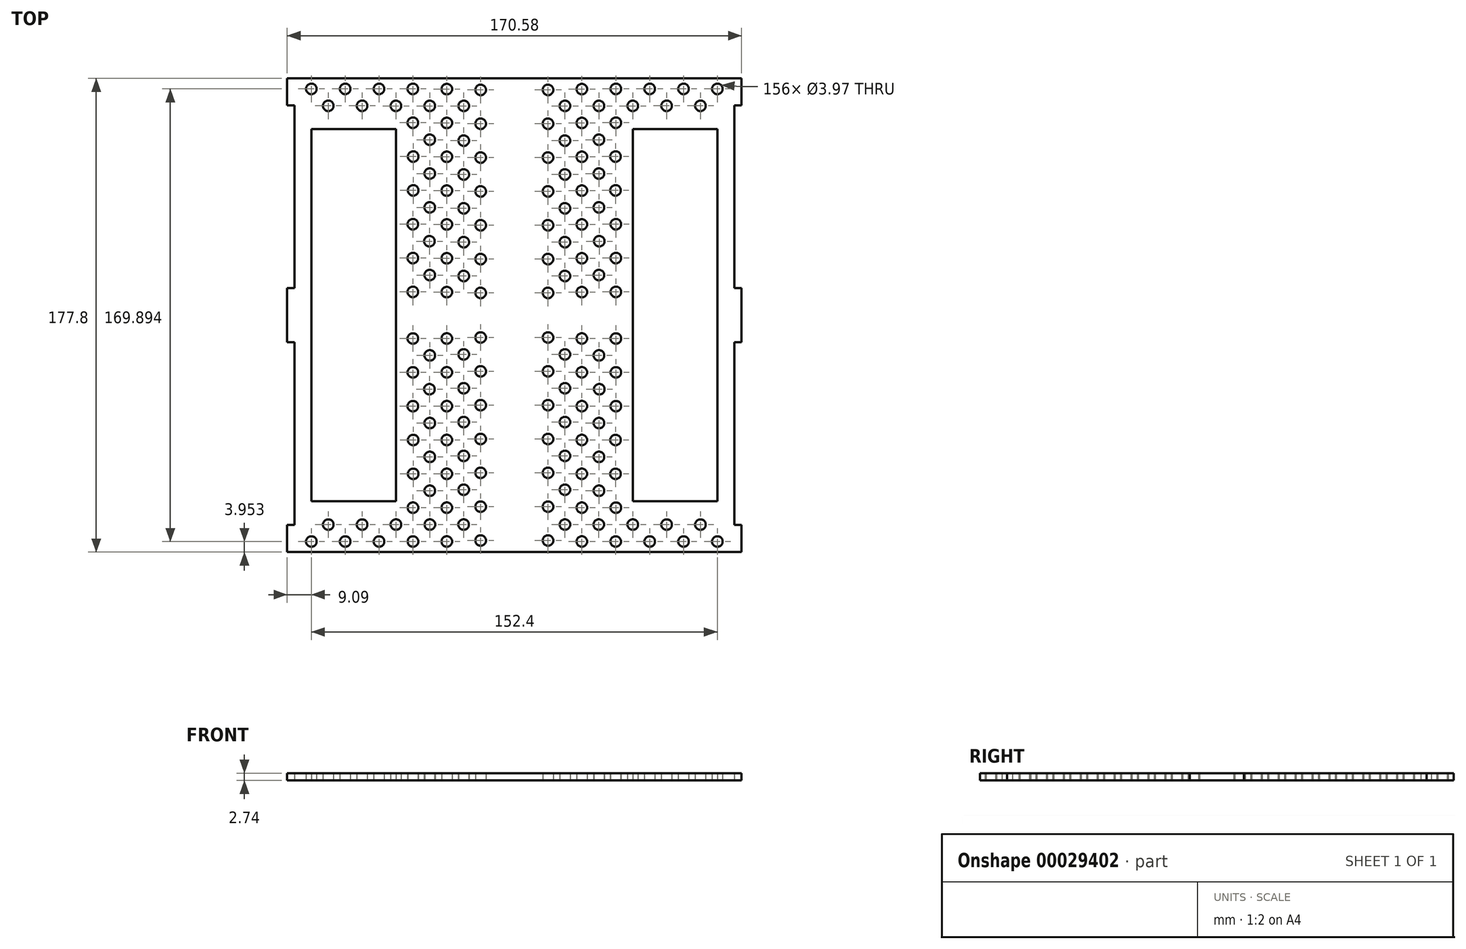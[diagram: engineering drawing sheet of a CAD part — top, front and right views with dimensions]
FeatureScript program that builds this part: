
annotation { "Feature Type Name" : "Feature", "Feature Type Description" : "" }
export const myFeature = defineFeature(function(context is Context, id is Id, definition is map)
    precondition{}
    {
        {
            var Q0;
            Q0=qCreatedBy(makeId("Top.planeOp"),FACE);
            var sketch = newSketch(context, id + "F0", { "sketchPlane" : qUnion([Q0])});
            skLineSegment(sketch, "E0.top", {"start": v(-63.5, -88.9) * mm, "end": v(19.05, -88.9) * mm});
            skLineSegment(sketch, "E1", {"start": v(-63.5, -88.9) * mm, "end": v(-66.24, -88.9) * mm});
            skLineSegment(sketch, "E2", {"start": v(-66.24, -88.9) * mm, "end": v(-66.24, -78.74) * mm});
            skLineSegment(sketch, "E3", {"start": v(-66.24, -78.74) * mm, "end": v(-63.5, -78.74) * mm});
            skLineSegment(sketch, "E4", {"start": v(-66.24, 0) * mm, "end": v(-66.24, -10.16) * mm});
            skLineSegment(sketch, "E5", {"start": v(-66.24, -10.16) * mm, "end": v(-63.5, -10.16) * mm});
            skLineSegment(sketch, "E6", {"start": v(-57.15, -69.85) * mm, "end": v(-57.15, 0) * mm});
            skLineSegment(sketch, "E7", {"start": v(-57.15, -69.85) * mm, "end": v(-25.4, -69.85) * mm});
            skLineSegment(sketch, "E8", {"start": v(-25.4, -69.85) * mm, "end": v(-25.4, 0) * mm});
            skLineSegment(sketch, "E9.trimOffspring", {"start": v(-63.5, -10.16) * mm, "end": v(-63.5, -78.74) * mm});
            skCircle(sketch, "E10.MirrorC", {"center": v(-57.15, -84.95) * mm, "radius": 1.98 * mm});
            skCircle(sketch, "E11.MirrorC", {"center": v(-44.45, -84.95) * mm, "radius": 1.98 * mm});
            skCircle(sketch, "E12.MirrorC", {"center": v(-31.75, -84.95) * mm, "radius": 1.98 * mm});
            skCircle(sketch, "E13.MirrorC", {"center": v(-19, -84.95) * mm, "radius": 1.98 * mm});
            skCircle(sketch, "E14.MirrorC", {"center": v(-19, -72.23) * mm, "radius": 1.98 * mm});
            skCircle(sketch, "E15.MirrorC", {"center": v(-50.8, -78.6) * mm, "radius": 1.98 * mm});
            skCircle(sketch, "E16.MirrorC", {"center": v(-38.1, -78.6) * mm, "radius": 1.98 * mm});
            skCircle(sketch, "E17.MirrorC", {"center": v(-25.4, -78.57) * mm, "radius": 1.98 * mm});
            skCircle(sketch, "E18.MirrorC", {"center": v(-12.64, -78.57) * mm, "radius": 1.98 * mm});
            skCircle(sketch, "E19.MirrorC", {"center": v(-18.92, -59.55) * mm, "radius": 1.98 * mm});
            skCircle(sketch, "E20.MirrorC", {"center": v(-18.92, -46.85) * mm, "radius": 1.98 * mm});
            skCircle(sketch, "E21.MirrorC", {"center": v(-19.05, -34.15) * mm, "radius": 1.98 * mm});
            skCircle(sketch, "E22.MirrorC", {"center": v(-19.05, -21.45) * mm, "radius": 1.98 * mm});
            skCircle(sketch, "E23.MirrorC", {"center": v(-19.05, -8.75) * mm, "radius": 1.98 * mm});
            skCircle(sketch, "E24.MirrorC", {"center": v(-12.7, -65.87) * mm, "radius": 1.98 * mm});
            skCircle(sketch, "E25.MirrorC", {"center": v(-12.7, -53.17) * mm, "radius": 1.98 * mm});
            skCircle(sketch, "E26.MirrorC", {"center": v(-12.7, -40.47) * mm, "radius": 1.98 * mm});
            skCircle(sketch, "E27.MirrorC", {"center": v(-12.83, -27.78) * mm, "radius": 1.98 * mm});
            skCircle(sketch, "E28.MirrorC", {"center": v(-12.7, -15.08) * mm, "radius": 1.98 * mm});
            skLineSegment(sketch, "E29.MirrorCS", {"start": v(-66.24, 78.74) * mm, "end": v(-63.5, 78.74) * mm});
            skCircle(sketch, "E30.MirrorC", {"center": v(-12.7, 78.57) * mm, "radius": 1.98 * mm});
            skLineSegment(sketch, "E31.MirrorCS", {"start": v(-66.24, 10.16) * mm, "end": v(-63.5, 10.16) * mm});
            skLineSegment(sketch, "E32.MirrorCS", {"start": v(-63.5, 88.9) * mm, "end": v(-66.24, 88.9) * mm});
            skCircle(sketch, "E33.MirrorC", {"center": v(-18.92, 59.55) * mm, "radius": 1.98 * mm});
            skCircle(sketch, "E34.MirrorC", {"center": v(-19.05, 34.15) * mm, "radius": 1.98 * mm});
            skCircle(sketch, "E35.MirrorC", {"center": v(-44.45, 84.95) * mm, "radius": 1.98 * mm});
            skCircle(sketch, "E36.MirrorC", {"center": v(-57.15, 84.95) * mm, "radius": 1.98 * mm});
            skCircle(sketch, "E37.MirrorC", {"center": v(-19.05, 84.95) * mm, "radius": 1.98 * mm});
            skCircle(sketch, "E38.MirrorC", {"center": v(-31.75, 84.95) * mm, "radius": 1.98 * mm});
            skCircle(sketch, "E39.MirrorC", {"center": v(-19.05, 21.45) * mm, "radius": 1.98 * mm});
            skCircle(sketch, "E40.MirrorC", {"center": v(-38.1, 78.6) * mm, "radius": 1.98 * mm});
            skCircle(sketch, "E41.MirrorC", {"center": v(-12.7, 15.08) * mm, "radius": 1.98 * mm});
            skCircle(sketch, "E42.MirrorC", {"center": v(-18.92, 46.85) * mm, "radius": 1.98 * mm});
            skCircle(sketch, "E43.MirrorC", {"center": v(-25.4, 78.57) * mm, "radius": 1.98 * mm});
            skCircle(sketch, "E44.MirrorC", {"center": v(-12.7, 65.87) * mm, "radius": 1.98 * mm});
            skCircle(sketch, "E45.MirrorC", {"center": v(-12.7, 40.47) * mm, "radius": 1.98 * mm});
            skCircle(sketch, "E46.MirrorC", {"center": v(-19.05, 8.75) * mm, "radius": 1.98 * mm});
            skCircle(sketch, "E47.MirrorC", {"center": v(-50.8, 78.6) * mm, "radius": 1.98 * mm});
            skCircle(sketch, "E48.MirrorC", {"center": v(-12.83, 27.78) * mm, "radius": 1.98 * mm});
            skCircle(sketch, "E49.MirrorC", {"center": v(-12.7, 53.17) * mm, "radius": 1.98 * mm});
            skCircle(sketch, "E50.MirrorC", {"center": v(-19.05, 72.25) * mm, "radius": 1.98 * mm});
            skLineSegment(sketch, "E51.MirrorCS", {"start": v(-63.5, 10.16) * mm, "end": v(-63.5, 78.74) * mm});
            skLineSegment(sketch, "E52.MirrorCS", {"start": v(-66.24, 0) * mm, "end": v(-66.24, 10.16) * mm});
            skLineSegment(sketch, "E53.MirrorCS", {"start": v(-57.15, 69.85) * mm, "end": v(-57.15, 0) * mm});
            skLineSegment(sketch, "E54.MirrorCS", {"start": v(-63.5, 88.9) * mm, "end": v(19.05, 88.9) * mm});
            skLineSegment(sketch, "E55.MirrorCS", {"start": v(-57.15, 69.85) * mm, "end": v(-25.4, 69.85) * mm});
            skLineSegment(sketch, "E56.MirrorCS", {"start": v(-66.24, 88.9) * mm, "end": v(-66.24, 78.74) * mm});
            skLineSegment(sketch, "E57.MirrorCS", {"start": v(-25.4, 69.85) * mm, "end": v(-25.4, 0) * mm});
            skPoint(sketch, "E58.MirrorCS.end.orphan", {"position": v(0, 0) * mm});
            skCircle(sketch, "E59.MirrorC", {"center": v(-6.3, -84.93) * mm, "radius": 1.98 * mm});
            skCircle(sketch, "E60.MirrorC", {"center": v(-6.3, -72.23) * mm, "radius": 1.98 * mm});
            skCircle(sketch, "E61.MirrorC", {"center": v(-6.3, -59.53) * mm, "radius": 1.98 * mm});
            skCircle(sketch, "E62.MirrorC", {"center": v(-6.3, -46.83) * mm, "radius": 1.98 * mm});
            skCircle(sketch, "E63.MirrorC", {"center": v(-6.3, -34.13) * mm, "radius": 1.98 * mm});
            skCircle(sketch, "E64.MirrorC", {"center": v(-6.3, -21.43) * mm, "radius": 1.98 * mm});
            skCircle(sketch, "E65.MirrorC", {"center": v(-6.3, -8.73) * mm, "radius": 1.98 * mm});
            skCircle(sketch, "E66.MirrorC", {"center": v(-6.3, 8.67) * mm, "radius": 1.98 * mm});
            skCircle(sketch, "E67.MirrorC", {"center": v(-6.3, 21.37) * mm, "radius": 1.98 * mm});
            skCircle(sketch, "E68.MirrorC", {"center": v(-6.3, 34.07) * mm, "radius": 1.98 * mm});
            skCircle(sketch, "E69.MirrorC", {"center": v(-6.3, 46.77) * mm, "radius": 1.98 * mm});
            skCircle(sketch, "E70.MirrorC", {"center": v(-6.3, 59.47) * mm, "radius": 1.98 * mm});
            skCircle(sketch, "E71.MirrorC", {"center": v(-6.3, 72.17) * mm, "radius": 1.98 * mm});
            skCircle(sketch, "E72.MirrorC", {"center": v(-6.3, 84.87) * mm, "radius": 1.98 * mm});
            skLineSegment(sketch, "E73.MirrorCS", {"start": v(101.6, -88.9) * mm, "end": v(104.34, -88.9) * mm});
            skLineSegment(sketch, "E74.MirrorCS", {"start": v(101.6, 88.9) * mm, "end": v(104.34, 88.9) * mm});
            skLineSegment(sketch, "E75.MirrorCS", {"start": v(104.34, -78.74) * mm, "end": v(101.6, -78.74) * mm});
            skLineSegment(sketch, "E76.MirrorCS", {"start": v(104.34, -10.16) * mm, "end": v(101.6, -10.16) * mm});
            skLineSegment(sketch, "E77.MirrorCS", {"start": v(104.34, 10.16) * mm, "end": v(101.6, 10.16) * mm});
            skLineSegment(sketch, "E78.MirrorCS", {"start": v(104.34, 78.74) * mm, "end": v(101.6, 78.74) * mm});
            skCircle(sketch, "E79.MirrorC", {"center": v(88.9, -78.6) * mm, "radius": 1.98 * mm});
            skCircle(sketch, "E80.MirrorC", {"center": v(44.4, -8.73) * mm, "radius": 1.98 * mm});
            skCircle(sketch, "E81.MirrorC", {"center": v(57.02, 46.85) * mm, "radius": 1.98 * mm});
            skCircle(sketch, "E82.MirrorC", {"center": v(50.8, -15.08) * mm, "radius": 1.98 * mm});
            skCircle(sketch, "E83.MirrorC", {"center": v(50.93, 27.78) * mm, "radius": 1.98 * mm});
            skCircle(sketch, "E84.MirrorC", {"center": v(57.15, -8.75) * mm, "radius": 1.98 * mm});
            skCircle(sketch, "E85.MirrorC", {"center": v(44.4, 46.77) * mm, "radius": 1.98 * mm});
            skCircle(sketch, "E86.MirrorC", {"center": v(57.1, -84.95) * mm, "radius": 1.98 * mm});
            skCircle(sketch, "E87.MirrorC", {"center": v(57.15, 34.15) * mm, "radius": 1.98 * mm});
            skCircle(sketch, "E88.MirrorC", {"center": v(57.15, 84.95) * mm, "radius": 1.98 * mm});
            skCircle(sketch, "E89.MirrorC", {"center": v(76.2, -78.6) * mm, "radius": 1.98 * mm});
            skCircle(sketch, "E90.MirrorC", {"center": v(44.4, -46.83) * mm, "radius": 1.98 * mm});
            skCircle(sketch, "E91.MirrorC", {"center": v(95.25, -84.95) * mm, "radius": 1.98 * mm});
            skCircle(sketch, "E92.MirrorC", {"center": v(57.15, 8.75) * mm, "radius": 1.98 * mm});
            skCircle(sketch, "E93.MirrorC", {"center": v(82.55, -84.95) * mm, "radius": 1.98 * mm});
            skCircle(sketch, "E94.MirrorC", {"center": v(63.5, -78.57) * mm, "radius": 1.98 * mm});
            skCircle(sketch, "E95.MirrorC", {"center": v(88.9, 78.6) * mm, "radius": 1.98 * mm});
            skCircle(sketch, "E96.MirrorC", {"center": v(69.85, 84.95) * mm, "radius": 1.98 * mm});
            skCircle(sketch, "E97.MirrorC", {"center": v(50.8, 53.17) * mm, "radius": 1.98 * mm});
            skCircle(sketch, "E98.MirrorC", {"center": v(57.02, -46.85) * mm, "radius": 1.98 * mm});
            skCircle(sketch, "E99.MirrorC", {"center": v(50.8, -65.87) * mm, "radius": 1.98 * mm});
            skCircle(sketch, "E100.MirrorC", {"center": v(82.55, 84.95) * mm, "radius": 1.98 * mm});
            skCircle(sketch, "E101.MirrorC", {"center": v(44.4, 59.47) * mm, "radius": 1.98 * mm});
            skCircle(sketch, "E102.MirrorC", {"center": v(44.4, 84.87) * mm, "radius": 1.98 * mm});
            skCircle(sketch, "E103.MirrorC", {"center": v(76.2, 78.6) * mm, "radius": 1.98 * mm});
            skCircle(sketch, "E104.MirrorC", {"center": v(44.4, -84.93) * mm, "radius": 1.98 * mm});
            skCircle(sketch, "E105.MirrorC", {"center": v(44.4, -34.13) * mm, "radius": 1.98 * mm});
            skCircle(sketch, "E106.MirrorC", {"center": v(50.8, -40.47) * mm, "radius": 1.98 * mm});
            skCircle(sketch, "E107.MirrorC", {"center": v(44.4, -59.53) * mm, "radius": 1.98 * mm});
            skCircle(sketch, "E108.MirrorC", {"center": v(57.15, 21.45) * mm, "radius": 1.98 * mm});
            skCircle(sketch, "E109.MirrorC", {"center": v(50.8, -53.17) * mm, "radius": 1.98 * mm});
            skCircle(sketch, "E110.MirrorC", {"center": v(50.74, -78.57) * mm, "radius": 1.98 * mm});
            skCircle(sketch, "E111.MirrorC", {"center": v(44.4, -21.43) * mm, "radius": 1.98 * mm});
            skCircle(sketch, "E112.MirrorC", {"center": v(57.02, 59.55) * mm, "radius": 1.98 * mm});
            skPoint(sketch, "E113.MirrorP", {"position": v(38.1, 0) * mm});
            skCircle(sketch, "E114.MirrorC", {"center": v(57.02, -59.55) * mm, "radius": 1.98 * mm});
            skCircle(sketch, "E115.MirrorC", {"center": v(69.85, -84.95) * mm, "radius": 1.98 * mm});
            skCircle(sketch, "E116.MirrorC", {"center": v(44.4, 8.67) * mm, "radius": 1.98 * mm});
            skCircle(sketch, "E117.MirrorC", {"center": v(63.5, 78.57) * mm, "radius": 1.98 * mm});
            skCircle(sketch, "E118.MirrorC", {"center": v(57.15, 72.25) * mm, "radius": 1.98 * mm});
            skCircle(sketch, "E119.MirrorC", {"center": v(95.25, 84.95) * mm, "radius": 1.98 * mm});
            skCircle(sketch, "E120.MirrorC", {"center": v(57.15, -34.15) * mm, "radius": 1.98 * mm});
            skCircle(sketch, "E121.MirrorC", {"center": v(44.4, 21.37) * mm, "radius": 1.98 * mm});
            skCircle(sketch, "E122.MirrorC", {"center": v(44.4, 72.17) * mm, "radius": 1.98 * mm});
            skCircle(sketch, "E123.MirrorC", {"center": v(57.15, -72.25) * mm, "radius": 1.98 * mm});
            skCircle(sketch, "E124.MirrorC", {"center": v(50.8, 65.87) * mm, "radius": 1.98 * mm});
            skCircle(sketch, "E125.MirrorC", {"center": v(50.8, 78.57) * mm, "radius": 1.98 * mm});
            skCircle(sketch, "E126.MirrorC", {"center": v(44.4, 34.07) * mm, "radius": 1.98 * mm});
            skCircle(sketch, "E127.MirrorC", {"center": v(50.8, 40.47) * mm, "radius": 1.98 * mm});
            skCircle(sketch, "E128.MirrorC", {"center": v(44.4, -72.23) * mm, "radius": 1.98 * mm});
            skCircle(sketch, "E129.MirrorC", {"center": v(50.8, 15.08) * mm, "radius": 1.98 * mm});
            skCircle(sketch, "E130.MirrorC", {"center": v(50.93, -27.78) * mm, "radius": 1.98 * mm});
            skCircle(sketch, "E131.MirrorC", {"center": v(57.15, -21.45) * mm, "radius": 1.98 * mm});
            skLineSegment(sketch, "E132.MirrorCS", {"start": v(104.34, 0) * mm, "end": v(104.34, 10.16) * mm});
            skLineSegment(sketch, "E133.MirrorCS", {"start": v(63.5, -69.85) * mm, "end": v(63.5, 0) * mm});
            skLineSegment(sketch, "E134.MirrorCS", {"start": v(101.6, -10.16) * mm, "end": v(101.6, -78.74) * mm});
            skLineSegment(sketch, "E135.MirrorCS", {"start": v(101.6, -88.9) * mm, "end": v(19.05, -88.9) * mm});
            skLineSegment(sketch, "E136.MirrorCS", {"start": v(95.25, 69.85) * mm, "end": v(95.25, 0) * mm});
            skLineSegment(sketch, "E137.MirrorCS", {"start": v(104.34, -88.9) * mm, "end": v(104.34, -78.74) * mm});
            skLineSegment(sketch, "E138.MirrorCS", {"start": v(104.34, 0) * mm, "end": v(104.34, -10.16) * mm});
            skLineSegment(sketch, "E139.MirrorCS", {"start": v(95.25, 69.85) * mm, "end": v(63.5, 69.85) * mm});
            skLineSegment(sketch, "E140.MirrorCS", {"start": v(95.25, -69.85) * mm, "end": v(95.25, 0) * mm});
            skLineSegment(sketch, "E141.MirrorCS", {"start": v(104.34, 88.9) * mm, "end": v(104.34, 78.74) * mm});
            skLineSegment(sketch, "E142.MirrorCS", {"start": v(95.25, -69.85) * mm, "end": v(63.5, -69.85) * mm});
            skLineSegment(sketch, "E143.MirrorCS", {"start": v(101.6, 88.9) * mm, "end": v(19.05, 88.9) * mm});
            skLineSegment(sketch, "E144.MirrorCS", {"start": v(101.6, 10.16) * mm, "end": v(101.6, 78.74) * mm});
            skLineSegment(sketch, "E145.MirrorCS", {"start": v(63.5, 69.85) * mm, "end": v(63.5, 0) * mm});
            skCircle(sketch, "E146.MirrorC", {"center": v(6.4, -84.57) * mm, "radius": 1.98 * mm});
            skCircle(sketch, "E147.MirrorC", {"center": v(0, -78.57) * mm, "radius": 1.98 * mm});
            skCircle(sketch, "E148.MirrorC", {"center": v(6.4, -71.87) * mm, "radius": 1.98 * mm});
            skCircle(sketch, "E149.MirrorC", {"center": v(0.06, -65.5) * mm, "radius": 1.98 * mm});
            skCircle(sketch, "E150.MirrorC", {"center": v(6.4, -59.17) * mm, "radius": 1.98 * mm});
            skCircle(sketch, "E151.MirrorC", {"center": v(0.06, -52.8) * mm, "radius": 1.98 * mm});
            skCircle(sketch, "E152.MirrorC", {"center": v(6.4, -46.47) * mm, "radius": 1.98 * mm});
            skCircle(sketch, "E153.MirrorC", {"center": v(0.06, -40.1) * mm, "radius": 1.98 * mm});
            skCircle(sketch, "E154.MirrorC", {"center": v(6.4, -33.77) * mm, "radius": 1.98 * mm});
            skCircle(sketch, "E155.MirrorC", {"center": v(0.06, -27.4) * mm, "radius": 1.98 * mm});
            skCircle(sketch, "E156.MirrorC", {"center": v(6.4, -21.07) * mm, "radius": 1.98 * mm});
            skCircle(sketch, "E157.MirrorC", {"center": v(0.06, -14.7) * mm, "radius": 1.98 * mm});
            skCircle(sketch, "E158.MirrorC", {"center": v(6.4, -8.37) * mm, "radius": 1.98 * mm});
            skCircle(sketch, "E159.MirrorC", {"center": v(6.4, 8.37) * mm, "radius": 1.98 * mm});
            skCircle(sketch, "E160.MirrorC", {"center": v(6.4, 84.57) * mm, "radius": 1.98 * mm});
            skCircle(sketch, "E161.MirrorC", {"center": v(6.4, 46.47) * mm, "radius": 1.98 * mm});
            skCircle(sketch, "E162.MirrorC", {"center": v(6.4, 71.87) * mm, "radius": 1.98 * mm});
            skCircle(sketch, "E163.MirrorC", {"center": v(6.4, 21.07) * mm, "radius": 1.98 * mm});
            skCircle(sketch, "E164.MirrorC", {"center": v(6.4, 59.17) * mm, "radius": 1.98 * mm});
            skCircle(sketch, "E165.MirrorC", {"center": v(6.4, 33.77) * mm, "radius": 1.98 * mm});
            skCircle(sketch, "E166.MirrorC", {"center": v(0.06, 65.5) * mm, "radius": 1.98 * mm});
            skCircle(sketch, "E167.MirrorC", {"center": v(0.06, 14.7) * mm, "radius": 1.98 * mm});
            skCircle(sketch, "E168.MirrorC", {"center": v(0.06, 27.4) * mm, "radius": 1.98 * mm});
            skCircle(sketch, "E169.MirrorC", {"center": v(0.06, 52.8) * mm, "radius": 1.98 * mm});
            skCircle(sketch, "E170.MirrorC", {"center": v(0.06, 78.57) * mm, "radius": 1.98 * mm});
            skCircle(sketch, "E171.MirrorC", {"center": v(0.06, 40.1) * mm, "radius": 1.98 * mm});
            skCircle(sketch, "E172.MirrorC", {"center": v(31.7, -8.37) * mm, "radius": 1.98 * mm});
            skCircle(sketch, "E173.MirrorC", {"center": v(31.7, 8.37) * mm, "radius": 1.98 * mm});
            skCircle(sketch, "E174.MirrorC", {"center": v(31.7, 46.47) * mm, "radius": 1.98 * mm});
            skCircle(sketch, "E175.MirrorC", {"center": v(31.7, 84.57) * mm, "radius": 1.98 * mm});
            skCircle(sketch, "E176.MirrorC", {"center": v(31.7, 71.87) * mm, "radius": 1.98 * mm});
            skCircle(sketch, "E177.MirrorC", {"center": v(31.7, -71.87) * mm, "radius": 1.98 * mm});
            skCircle(sketch, "E178.MirrorC", {"center": v(31.7, 21.07) * mm, "radius": 1.98 * mm});
            skCircle(sketch, "E179.MirrorC", {"center": v(31.7, -21.07) * mm, "radius": 1.98 * mm});
            skCircle(sketch, "E180.MirrorC", {"center": v(31.7, 59.17) * mm, "radius": 1.98 * mm});
            skCircle(sketch, "E181.MirrorC", {"center": v(31.7, 33.77) * mm, "radius": 1.98 * mm});
            skCircle(sketch, "E182.MirrorC", {"center": v(31.7, -59.17) * mm, "radius": 1.98 * mm});
            skCircle(sketch, "E183.MirrorC", {"center": v(31.7, -46.47) * mm, "radius": 1.98 * mm});
            skCircle(sketch, "E184.MirrorC", {"center": v(31.7, -33.77) * mm, "radius": 1.98 * mm});
            skCircle(sketch, "E185.MirrorC", {"center": v(31.7, -84.57) * mm, "radius": 1.98 * mm});
            skCircle(sketch, "E186.MirrorC", {"center": v(38.04, -78.57) * mm, "radius": 1.98 * mm});
            skCircle(sketch, "E187.MirrorC", {"center": v(38.04, -65.5) * mm, "radius": 1.98 * mm});
            skCircle(sketch, "E188.MirrorC", {"center": v(38.04, -52.8) * mm, "radius": 1.98 * mm});
            skCircle(sketch, "E189.MirrorC", {"center": v(38.04, -40.1) * mm, "radius": 1.98 * mm});
            skCircle(sketch, "E190.MirrorC", {"center": v(38.04, -27.4) * mm, "radius": 1.98 * mm});
            skCircle(sketch, "E191.MirrorC", {"center": v(38.04, -14.7) * mm, "radius": 1.98 * mm});
            skCircle(sketch, "E192.MirrorC", {"center": v(38.04, 14.7) * mm, "radius": 1.98 * mm});
            skCircle(sketch, "E193.MirrorC", {"center": v(38.04, 27.4) * mm, "radius": 1.98 * mm});
            skCircle(sketch, "E194.MirrorC", {"center": v(38.04, 40.1) * mm, "radius": 1.98 * mm});
            skCircle(sketch, "E195.MirrorC", {"center": v(38.04, 52.8) * mm, "radius": 1.98 * mm});
            skCircle(sketch, "E196.MirrorC", {"center": v(38.04, 65.5) * mm, "radius": 1.98 * mm});
            skCircle(sketch, "E197.MirrorC", {"center": v(38.04, 78.57) * mm, "radius": 1.98 * mm});
            skSolve(sketch);
        }
        {
            var Q0;
            Q0=makeQuery(id+"F0.imprint","IMPRINT",FACE,{"disambiguationData":[TD([[makeQuery(id+"F0.imprint","IMPRINT",EDGE,{"derivedFrom":sQuery(id+"F0.wireOp",EDGE,"E0.top")}),1.0]])]});
            extrude(context, id + "F1", {"entities" : qUnion([Q0]), "depth" : 2.74 * mm});
        }
    });
